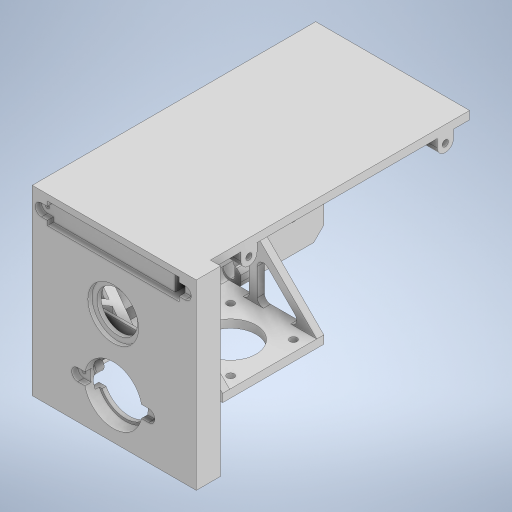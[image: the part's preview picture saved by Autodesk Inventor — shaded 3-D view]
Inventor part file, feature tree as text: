
AUTODESK INVENTOR PART (.ipt)
format: ipt  version: 2023 (Build 270158000, 158)  size: 761,344 bytes
history: native  units: mm
features: extrude x30, sketch x27, fillet x8, chamfer x7, other x6, mirror x2, revolve x2
ambient origin geometry x8: Origin, YZ Plane, XZ Plane, XY Plane, X Axis, Y Axis, Z Axis, Center Point
bodies: Body1 (feature_tree)
feature tree (82):
  other  "솔리드1"
  sketch  "스케치1"
  extrude  "돌출1"  Depth=90.0mm
  extrude  "돌출2"  Depth=140.0mm
  extrude  "돌출3"  Depth=4.0mm TaperAngle=0.0deg
  extrude  "돌출5"  Depth=72.0mm TaperAngle=0.0deg
  extrude  "돌출6"  Depth=4.0mm
  other  "작업 평면1"
  mirror  "미러1"
  extrude  "돌출7"  Depth=4.0mm
  extrude  "돌출8"  Depth=10.0mm
  extrude  "돌출9"  Depth=10.0mm
  extrude  "돌출10"  Depth=10.0mm
  extrude  "돌출11"  Depth=10.0mm
  sketch  "스케치11"
  extrude  "돌출12"  Depth=4.0mm
  extrude  "돌출13"  Depth=10.0mm TaperAngle=0.0deg
  extrude  "돌출14"  Depth=6.0mm
  chamfer  "모따기2"  Distance=36.0mm
  chamfer  "모따기3"  Distance=8.0mm
  extrude  "돌출15"  Depth=50.0mm
  fillet  "모깎기2"  Radius=10.0mm
  other  "작업 평면2"
  sketch  "스케치17"
  revolve  "회전1"
  revolve  "회전2"
  extrude  "돌출16"  Depth=46.0mm TaperAngle=0.0deg
  sketch  "스케치19"
  extrude  "돌출17"  Depth=30.0mm
  extrude  "돌출18"  TaperAngle=30.0deg  [1 undecoded]
  extrude  "돌출19"  Depth=4.0mm
  fillet  "모깎기3"  Radius=2.0mm
  other  "작업 평면3"
  extrude  "돌출20"  Depth=2.0mm
  extrude  "돌출21"  Depth=4.0mm TaperAngle=0.0deg
  extrude  "돌출22"  Depth=2.0mm
  other  "작업 평면4"
  fillet  "모깎기4"  Radius=40.0mm
  mirror  "미러2"
  chamfer  "모따기4"  Distance=20.0mm
  extrude  "돌출23"  Depth=20.0mm
  extrude  "돌출24"  Depth=36.0mm
  chamfer  "모따기5"  Distance=20.0mm
  extrude  "돌출25"  Depth=20.0mm TaperAngle=0.0deg
  chamfer  "모따기6"  Distance=5.0mm
  extrude  "돌출26"  Depth=5.0mm TaperAngle=0.0deg
  fillet  "모깎기5"  Radius=65.0mm
  extrude  "돌출27"  Depth=10.5mm
  chamfer  "모따기7"  Distance=3.0mm
  extrude  "돌출28"  Depth=3.0mm TaperAngle=0.0deg
  fillet  "모깎기6"  Radius=2.0mm
  other  "작업 평면5"
  extrude  "돌출29"  Depth=6.0mm
  fillet  "모깎기7"  Radius=3.0mm
  fillet  "모깎기8"  Radius=10.0mm
  chamfer  "모따기8"  Distance=55.0mm
  fillet  "모깎기9"  Radius=10.0mm
  extrude  "돌출30"  Depth=1.0mm TaperAngle=45.0deg
  extrude  "돌출31"  Depth=1.0mm TaperAngle=45.0deg
  sketch  "스케치2"
  sketch  "스케치3"
  sketch  "스케치4"
  sketch  "스케치5"
  sketch  "스케치6"
  sketch  "스케치7"
  sketch  "스케치9"
  sketch  "스케치10"
  sketch  "스케치12"
  sketch  "스케치14"
  sketch  "스케치18"
  sketch  "스케치20"
  sketch  "스케치21"
  sketch  "스케치22"
  sketch  "스케치25"
  sketch  "스케치26"
  sketch  "스케치27"
  sketch  "스케치28"
  sketch  "스케치29"
  sketch  "스케치30"
  sketch  "스케치31"
  sketch  "스케치33"
  sketch  "스케치34"
note: 1 required parameter value undecoded (feature->parameter linkage not recoverable at this tier; creation-order binding heuristic only, values carry confidence <= 0.55)
